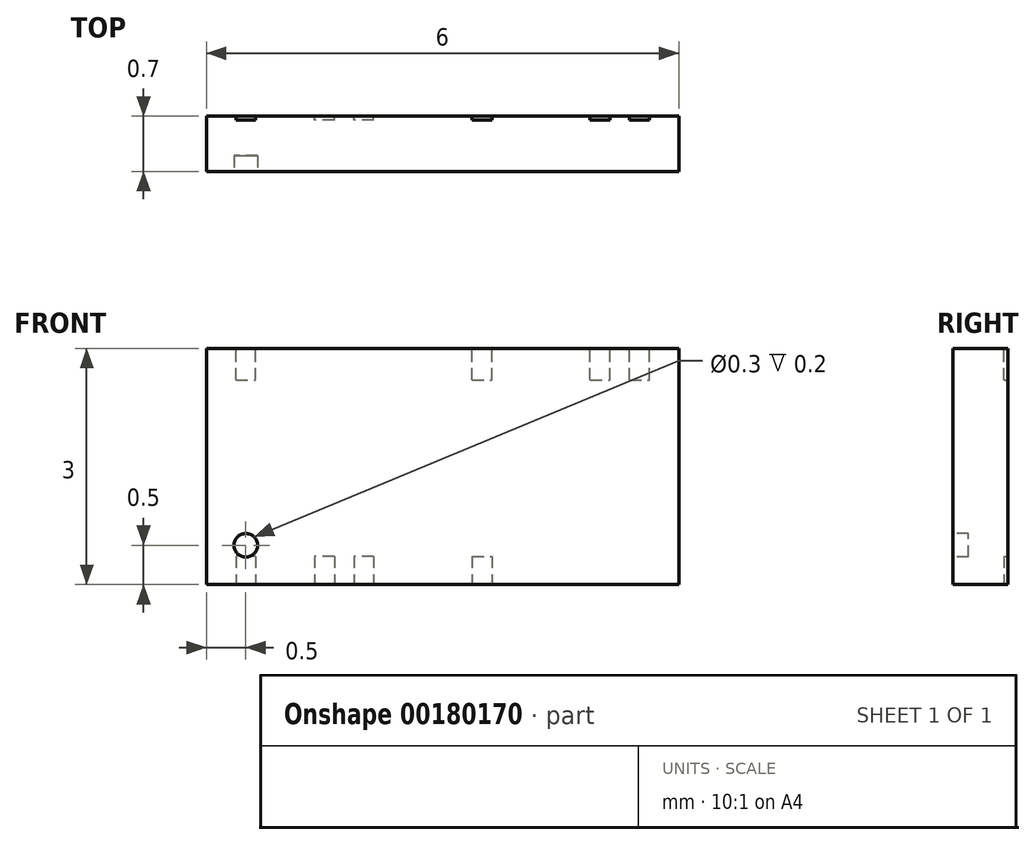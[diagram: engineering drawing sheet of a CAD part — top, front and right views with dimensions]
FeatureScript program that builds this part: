
annotation { "Feature Type Name" : "Feature", "Feature Type Description" : "" }
export const myFeature = defineFeature(function(context is Context, id is Id, definition is map)
    precondition{}
    {
        {
            var Q0;
            Q0=qCreatedBy(makeId("Front.planeOp"),FACE);
            var sketch = newSketch(context, id + "F0", { "sketchPlane" : qUnion([Q0])});
            skLineSegment(sketch, "E0.bottom", {"start": v(3, 1.5) * mm, "end": v(-3, 1.5) * mm});
            skLineSegment(sketch, "E0.top", {"start": v(3, -1.5) * mm, "end": v(-3, -1.5) * mm});
            skLineSegment(sketch, "E0.left", {"start": v(3, 1.5) * mm, "end": v(3, -1.5) * mm});
            skLineSegment(sketch, "E0.right", {"start": v(-3, 1.5) * mm, "end": v(-3, -1.5) * mm});
            skPoint(sketch, "E0.middle", {"position": v(0, 0) * mm});
            skSolve(sketch);
        }
        {
            var Q0;
            Q0 = qSketchRegion(id + "F0", true);
            extrude(context, id + "F1", {"entities" : qUnion([Q0]), "depth" : 0.7 * mm});
        }
        {
            var Q0;
            Q0=makeQuery(id+"F1.opExtrude","CAP_FACE",FACE,{"disambiguationData":[OSD([sQuery(id+"F0.wireOp",EDGE,"E0.bottom"),sQuery(id+"F0.wireOp",EDGE,"E0.top"),sQuery(id+"F0.wireOp",EDGE,"E0.left"),sQuery(id+"F0.wireOp",EDGE,"E0.right")])],"isStart":false});
            var sketch = newSketch(context, id + "F2", { "sketchPlane" : qUnion([Q0])});
            skCircle(sketch, "E1", {"center": v(-2.5, -1) * mm, "radius": 0.15 * mm});
            skSolve(sketch);
        }
        {
            var Q0;
            Q0 = qSketchRegion(id + "F2", true);
            extrude(context, id + "F3", {"entities" : qUnion([Q0]), "operationType" : NewBodyOperationType.REMOVE, "oppositeDirection" : true, "depth" : 0.2 * mm});
        }
        {
            var Q0;
            Q0=makeQuery(id+"F1.opExtrude","CAP_FACE",FACE,{"disambiguationData":[OSD([sQuery(id+"F0.wireOp",EDGE,"E0.bottom"),sQuery(id+"F0.wireOp",EDGE,"E0.top"),sQuery(id+"F0.wireOp",EDGE,"E0.left"),sQuery(id+"F0.wireOp",EDGE,"E0.right")])],"isStart":true});
            var sketch = newSketch(context, id + "F4", { "sketchPlane" : qUnion([Q0])});
            skLineSegment(sketch, "E2.bottom", {"start": v(2.62, 1.1) * mm, "end": v(2.38, 1.1) * mm});
            skLineSegment(sketch, "E2.right", {"start": v(2.38, 1.1) * mm, "end": v(2.38, 1.5) * mm});
            skPoint(sketch, "E2.middle", {"position": v(2.5, 1.5) * mm});
            skLineSegment(sketch, "E3.bottom", {"start": v(2.37, -1.14) * mm, "end": v(2.62, -1.14) * mm});
            skLineSegment(sketch, "E3.left", {"start": v(2.38, -1.14) * mm, "end": v(2.38, -1.5) * mm});
            skPoint(sketch, "E3.middle", {"position": v(2.5, -1.5) * mm});
            skPoint(sketch, "E3.cornerSnap0", {"position": v(2.38, 1.5) * mm});
            skLineSegment(sketch, "E4.bottom", {"start": v(2.12, 1.1) * mm, "end": v(1.88, 1.1) * mm});
            skLineSegment(sketch, "E4.left", {"start": v(2.12, 1.1) * mm, "end": v(2.12, 1.5) * mm});
            skPoint(sketch, "E4.middle", {"position": v(2, 1.5) * mm});
            skLineSegment(sketch, "E5.bottom", {"start": v(1.88, -1.14) * mm, "end": v(2.13, -1.14) * mm});
            skLineSegment(sketch, "E5.left", {"start": v(1.88, -1.14) * mm, "end": v(1.88, -1.5) * mm});
            skPoint(sketch, "E5.middle", {"position": v(2, -1.5) * mm});
            skLineSegment(sketch, "E6.bottom", {"start": v(1.63, 1.1) * mm, "end": v(1.38, 1.1) * mm});
            skLineSegment(sketch, "E6.left", {"start": v(1.63, 1.1) * mm, "end": v(1.63, 1.5) * mm});
            skPoint(sketch, "E6.middle", {"position": v(1.5, 1.5) * mm});
            skLineSegment(sketch, "E7.bottom", {"start": v(1.38, -1.14) * mm, "end": v(1.62, -1.14) * mm});
            skLineSegment(sketch, "E7.left", {"start": v(1.38, -1.14) * mm, "end": v(1.38, -1.5) * mm});
            skPoint(sketch, "E7.middle", {"position": v(1.5, -1.5) * mm});
            skLineSegment(sketch, "E8.bottom", {"start": v(1.13, 1.1) * mm, "end": v(0.88, 1.1) * mm});
            skLineSegment(sketch, "E8.left", {"start": v(1.13, 1.1) * mm, "end": v(1.13, 1.5) * mm});
            skPoint(sketch, "E8.middle", {"position": v(1, 1.5) * mm});
            skLineSegment(sketch, "E9.bottom", {"start": v(0.88, -1.14) * mm, "end": v(1.13, -1.14) * mm});
            skLineSegment(sketch, "E9.left", {"start": v(0.87, -1.14) * mm, "end": v(0.87, -1.5) * mm});
            skPoint(sketch, "E9.middle", {"position": v(1, -1.5) * mm});
            skLineSegment(sketch, "E10.bottom", {"start": v(0.37, 1.1) * mm, "end": v(0.62, 1.1) * mm});
            skLineSegment(sketch, "E10.right", {"start": v(0.62, 1.1) * mm, "end": v(0.62, 1.5) * mm});
            skPoint(sketch, "E10.middle", {"position": v(0.5, 1.5) * mm});
            skLineSegment(sketch, "E11.bottom", {"start": v(0.38, -1.14) * mm, "end": v(0.62, -1.14) * mm});
            skLineSegment(sketch, "E11.left", {"start": v(0.38, -1.14) * mm, "end": v(0.38, -1.5) * mm});
            skPoint(sketch, "E11.middle", {"position": v(0.5, -1.5) * mm});
            skLineSegment(sketch, "E12.bottom", {"start": v(0.12, 1.1) * mm, "end": v(-0.13, 1.1) * mm});
            skLineSegment(sketch, "E12.left", {"start": v(0.13, 1.1) * mm, "end": v(0.13, 1.5) * mm});
            skPoint(sketch, "E12.middle", {"position": v(0, 1.5) * mm});
            skPoint(sketch, "E12.cornerSnap0", {"position": v(0.5, 1.1) * mm});
            skLineSegment(sketch, "E13.bottom", {"start": v(-0.12, -1.14) * mm, "end": v(0.13, -1.14) * mm});
            skLineSegment(sketch, "E13.left", {"start": v(-0.13, -1.14) * mm, "end": v(-0.13, -1.5) * mm});
            skPoint(sketch, "E13.middle", {"position": v(0, -1.5) * mm});
            skLineSegment(sketch, "E14.bottom", {"start": v(-0.38, 1.1) * mm, "end": v(-0.63, 1.1) * mm});
            skLineSegment(sketch, "E14.left", {"start": v(-0.37, 1.1) * mm, "end": v(-0.37, 1.5) * mm});
            skPoint(sketch, "E14.middle", {"position": v(-0.5, 1.5) * mm});
            skLineSegment(sketch, "E15.bottom", {"start": v(-0.37, -1.14) * mm, "end": v(-0.62, -1.14) * mm});
            skLineSegment(sketch, "E15.right", {"start": v(-0.62, -1.14) * mm, "end": v(-0.62, -1.5) * mm});
            skPoint(sketch, "E15.middle", {"position": v(-0.5, -1.5) * mm});
            skLineSegment(sketch, "E16.bottom", {"start": v(-0.88, 1.1) * mm, "end": v(-1.13, 1.1) * mm});
            skLineSegment(sketch, "E16.left", {"start": v(-0.88, 1.1) * mm, "end": v(-0.88, 1.5) * mm});
            skPoint(sketch, "E16.middle", {"position": v(-1, 1.5) * mm});
            skLineSegment(sketch, "E17.bottom", {"start": v(-0.87, -1.14) * mm, "end": v(-1.12, -1.14) * mm});
            skLineSegment(sketch, "E17.right", {"start": v(-1.12, -1.14) * mm, "end": v(-1.12, -1.5) * mm});
            skPoint(sketch, "E17.middle", {"position": v(-1, -1.5) * mm});
            skLineSegment(sketch, "E18.bottom", {"start": v(-1.38, 1.1) * mm, "end": v(-1.63, 1.1) * mm});
            skLineSegment(sketch, "E18.left", {"start": v(-1.38, 1.1) * mm, "end": v(-1.38, 1.5) * mm});
            skPoint(sketch, "E18.middle", {"position": v(-1.5, 1.5) * mm});
            skLineSegment(sketch, "E19.bottom", {"start": v(-1.37, -1.14) * mm, "end": v(-1.62, -1.14) * mm});
            skLineSegment(sketch, "E19.right", {"start": v(-1.62, -1.14) * mm, "end": v(-1.62, -1.5) * mm});
            skPoint(sketch, "E19.middle", {"position": v(-1.5, -1.5) * mm});
            skLineSegment(sketch, "E20.bottom", {"start": v(-1.88, 1.1) * mm, "end": v(-2.12, 1.1) * mm});
            skLineSegment(sketch, "E20.left", {"start": v(-1.88, 1.1) * mm, "end": v(-1.88, 1.5) * mm});
            skPoint(sketch, "E20.middle", {"position": v(-2, 1.5) * mm});
            skLineSegment(sketch, "E21.bottom", {"start": v(-1.88, -1.14) * mm, "end": v(-2.12, -1.14) * mm});
            skLineSegment(sketch, "E21.right", {"start": v(-2.12, -1.14) * mm, "end": v(-2.12, -1.5) * mm});
            skPoint(sketch, "E21.middle", {"position": v(-2, -1.5) * mm});
            skLineSegment(sketch, "E22.bottom", {"start": v(-2.38, 1.1) * mm, "end": v(-2.63, 1.1) * mm});
            skLineSegment(sketch, "E22.left", {"start": v(-2.37, 1.1) * mm, "end": v(-2.37, 1.5) * mm});
            skPoint(sketch, "E22.middle", {"position": v(-2.5, 1.5) * mm});
            skLineSegment(sketch, "E23.bottom", {"start": v(-2.37, -1.14) * mm, "end": v(-2.62, -1.14) * mm});
            skLineSegment(sketch, "E23.right", {"start": v(-2.62, -1.14) * mm, "end": v(-2.62, -1.5) * mm});
            skPoint(sketch, "E23.middle", {"position": v(-2.5, -1.5) * mm});
            skPoint(sketch, "E24.orphan", {"position": v(2.38, 1.9) * mm});
            skPoint(sketch, "E2.left.end.orphan", {"position": v(2.62, 1.9) * mm});
            skLineSegment(sketch, "E25.top", {"start": v(2.62, 1.5) * mm, "end": v(2.38, 1.5) * mm});
            skLineSegment(sketch, "E25.left", {"start": v(2.62, 1.1) * mm, "end": v(2.62, 1.5) * mm});
            skLineSegment(sketch, "E26.bottom", {"start": v(1.88, 1.1) * mm, "end": v(2.12, 1.1) * mm});
            skLineSegment(sketch, "E26.top", {"start": v(1.88, 1.5) * mm, "end": v(2.12, 1.5) * mm});
            skLineSegment(sketch, "E26.left", {"start": v(1.88, 1.1) * mm, "end": v(1.88, 1.5) * mm});
            skLineSegment(sketch, "E27.bottom", {"start": v(1.38, 1.1) * mm, "end": v(1.63, 1.1) * mm});
            skLineSegment(sketch, "E27.top", {"start": v(1.38, 1.5) * mm, "end": v(1.63, 1.5) * mm});
            skLineSegment(sketch, "E27.left", {"start": v(1.38, 1.1) * mm, "end": v(1.38, 1.5) * mm});
            skLineSegment(sketch, "E28.bottom", {"start": v(0.88, 1.1) * mm, "end": v(1.13, 1.1) * mm});
            skLineSegment(sketch, "E28.top", {"start": v(0.88, 1.5) * mm, "end": v(1.12, 1.5) * mm});
            skLineSegment(sketch, "E28.left", {"start": v(0.88, 1.1) * mm, "end": v(0.88, 1.5) * mm});
            skLineSegment(sketch, "E28.right", {"start": v(1.12, 1.1) * mm, "end": v(1.12, 1.5) * mm});
            skPoint(sketch, "E29.orphan", {"position": v(1.87, 1.9) * mm});
            skPoint(sketch, "E30.orphan", {"position": v(2.12, 1.9) * mm});
            skPoint(sketch, "E31.orphan", {"position": v(1.38, 1.9) * mm});
            skPoint(sketch, "E32.orphan", {"position": v(1.63, 1.9) * mm});
            skPoint(sketch, "E33.orphan", {"position": v(0.87, 1.9) * mm});
            skPoint(sketch, "E34.orphan", {"position": v(1.13, 1.9) * mm});
            skLineSegment(sketch, "E35.bottom", {"start": v(0.62, 1.1) * mm, "end": v(0.38, 1.1) * mm});
            skLineSegment(sketch, "E35.top", {"start": v(0.62, 1.5) * mm, "end": v(0.38, 1.5) * mm});
            skLineSegment(sketch, "E35.right", {"start": v(0.38, 1.1) * mm, "end": v(0.38, 1.5) * mm});
            skLineSegment(sketch, "E36.bottom", {"start": v(0.12, 1.1) * mm, "end": v(-0.12, 1.1) * mm});
            skLineSegment(sketch, "E36.top", {"start": v(0.12, 1.5) * mm, "end": v(-0.12, 1.5) * mm});
            skLineSegment(sketch, "E36.left", {"start": v(0.12, 1.1) * mm, "end": v(0.12, 1.5) * mm});
            skLineSegment(sketch, "E36.right", {"start": v(-0.12, 1.1) * mm, "end": v(-0.12, 1.5) * mm});
            skLineSegment(sketch, "E37.top", {"start": v(-0.38, 1.5) * mm, "end": v(-0.63, 1.5) * mm});
            skLineSegment(sketch, "E37.left", {"start": v(-0.38, 1.1) * mm, "end": v(-0.38, 1.5) * mm});
            skLineSegment(sketch, "E37.right", {"start": v(-0.63, 1.1) * mm, "end": v(-0.63, 1.5) * mm});
            skLineSegment(sketch, "E38.bottom", {"start": v(-0.88, 1.1) * mm, "end": v(-1.12, 1.1) * mm});
            skLineSegment(sketch, "E38.top", {"start": v(-0.87, 1.5) * mm, "end": v(-1.12, 1.5) * mm});
            skLineSegment(sketch, "E38.left", {"start": v(-0.87, 1.1) * mm, "end": v(-0.87, 1.5) * mm});
            skLineSegment(sketch, "E38.right", {"start": v(-1.12, 1.1) * mm, "end": v(-1.12, 1.5) * mm});
            skLineSegment(sketch, "E39.bottom", {"start": v(-1.38, 1.1) * mm, "end": v(-1.62, 1.1) * mm});
            skLineSegment(sketch, "E39.top", {"start": v(-1.38, 1.5) * mm, "end": v(-1.62, 1.5) * mm});
            skLineSegment(sketch, "E39.right", {"start": v(-1.62, 1.1) * mm, "end": v(-1.62, 1.5) * mm});
            skLineSegment(sketch, "E40.bottom", {"start": v(-1.88, 1.1) * mm, "end": v(-2.13, 1.1) * mm});
            skLineSegment(sketch, "E40.top", {"start": v(-1.88, 1.5) * mm, "end": v(-2.13, 1.5) * mm});
            skLineSegment(sketch, "E40.right", {"start": v(-2.13, 1.1) * mm, "end": v(-2.13, 1.5) * mm});
            skLineSegment(sketch, "E41.top", {"start": v(-2.38, 1.5) * mm, "end": v(-2.63, 1.5) * mm});
            skLineSegment(sketch, "E41.left", {"start": v(-2.38, 1.1) * mm, "end": v(-2.38, 1.5) * mm});
            skLineSegment(sketch, "E41.right", {"start": v(-2.63, 1.1) * mm, "end": v(-2.63, 1.5) * mm});
            skPoint(sketch, "E42.orphan", {"position": v(0.38, 1.9) * mm});
            skPoint(sketch, "E43.orphan", {"position": v(0.62, 1.9) * mm});
            skPoint(sketch, "E12.top.end.orphan", {"position": v(-0.12, 1.9) * mm});
            skPoint(sketch, "E44.orphan", {"position": v(0.13, 1.9) * mm});
            skPoint(sketch, "E45.orphan", {"position": v(-0.62, 1.9) * mm});
            skPoint(sketch, "E46.orphan", {"position": v(-0.37, 1.9) * mm});
            skPoint(sketch, "E47.orphan", {"position": v(-1.12, 1.9) * mm});
            skPoint(sketch, "E48.orphan", {"position": v(-0.88, 1.9) * mm});
            skPoint(sketch, "E49.orphan", {"position": v(-1.62, 1.9) * mm});
            skPoint(sketch, "E50.orphan", {"position": v(-1.38, 1.9) * mm});
            skPoint(sketch, "E51.orphan", {"position": v(-2.13, 1.9) * mm});
            skPoint(sketch, "E52.orphan", {"position": v(-1.88, 1.9) * mm});
            skPoint(sketch, "E53.orphan", {"position": v(-2.62, 1.9) * mm});
            skPoint(sketch, "E54.orphan", {"position": v(-2.37, 1.9) * mm});
            skLineSegment(sketch, "E55.bottom", {"start": v(2.37, -1.14) * mm, "end": v(2.63, -1.14) * mm});
            skLineSegment(sketch, "E55.top", {"start": v(2.37, -1.5) * mm, "end": v(2.63, -1.5) * mm});
            skLineSegment(sketch, "E55.left", {"start": v(2.37, -1.14) * mm, "end": v(2.37, -1.5) * mm});
            skLineSegment(sketch, "E55.right", {"start": v(2.63, -1.14) * mm, "end": v(2.63, -1.5) * mm});
            skLineSegment(sketch, "E56.bottom", {"start": v(1.88, -1.14) * mm, "end": v(2.12, -1.14) * mm});
            skLineSegment(sketch, "E56.top", {"start": v(1.88, -1.5) * mm, "end": v(2.12, -1.5) * mm});
            skLineSegment(sketch, "E56.right", {"start": v(2.12, -1.14) * mm, "end": v(2.12, -1.5) * mm});
            skLineSegment(sketch, "E57.top", {"start": v(1.38, -1.5) * mm, "end": v(1.62, -1.5) * mm});
            skLineSegment(sketch, "E57.right", {"start": v(1.62, -1.14) * mm, "end": v(1.62, -1.5) * mm});
            skLineSegment(sketch, "E58.top", {"start": v(0.88, -1.5) * mm, "end": v(1.13, -1.5) * mm});
            skLineSegment(sketch, "E58.left", {"start": v(0.88, -1.14) * mm, "end": v(0.88, -1.5) * mm});
            skLineSegment(sketch, "E58.right", {"start": v(1.13, -1.14) * mm, "end": v(1.13, -1.5) * mm});
            skLineSegment(sketch, "E59.top", {"start": v(0.38, -1.5) * mm, "end": v(0.62, -1.5) * mm});
            skLineSegment(sketch, "E59.right", {"start": v(0.62, -1.14) * mm, "end": v(0.62, -1.5) * mm});
            skLineSegment(sketch, "E60.bottom", {"start": v(-0.12, -1.14) * mm, "end": v(0.12, -1.14) * mm});
            skLineSegment(sketch, "E60.top", {"start": v(-0.12, -1.5) * mm, "end": v(0.12, -1.5) * mm});
            skLineSegment(sketch, "E60.left", {"start": v(-0.12, -1.14) * mm, "end": v(-0.12, -1.5) * mm});
            skLineSegment(sketch, "E60.right", {"start": v(0.12, -1.14) * mm, "end": v(0.12, -1.5) * mm});
            skPoint(sketch, "E61.orphan", {"position": v(2.62, -1.86) * mm});
            skPoint(sketch, "E62.orphan", {"position": v(2.38, -1.86) * mm});
            skPoint(sketch, "E63.orphan", {"position": v(2.12, -1.86) * mm});
            skPoint(sketch, "E64.orphan", {"position": v(1.88, -1.86) * mm});
            skPoint(sketch, "E65.orphan", {"position": v(1.62, -1.86) * mm});
            skPoint(sketch, "E66.orphan", {"position": v(1.38, -1.86) * mm});
            skPoint(sketch, "E67.orphan", {"position": v(1.13, -1.86) * mm});
            skPoint(sketch, "E68.orphan", {"position": v(0.87, -1.86) * mm});
            skPoint(sketch, "E69.orphan", {"position": v(0.62, -1.86) * mm});
            skPoint(sketch, "E70.orphan", {"position": v(0.38, -1.86) * mm});
            skPoint(sketch, "E13.top.end.orphan", {"position": v(0.13, -1.86) * mm});
            skPoint(sketch, "E71.orphan", {"position": v(-0.13, -1.86) * mm});
            skLineSegment(sketch, "E72.bottom", {"start": v(-0.62, -1.14) * mm, "end": v(-0.37, -1.14) * mm});
            skLineSegment(sketch, "E72.top", {"start": v(-0.62, -1.5) * mm, "end": v(-0.37, -1.5) * mm});
            skLineSegment(sketch, "E72.right", {"start": v(-0.37, -1.14) * mm, "end": v(-0.37, -1.5) * mm});
            skLineSegment(sketch, "E73.bottom", {"start": v(-1.12, -1.14) * mm, "end": v(-0.88, -1.14) * mm});
            skLineSegment(sketch, "E73.top", {"start": v(-1.12, -1.5) * mm, "end": v(-0.88, -1.5) * mm});
            skLineSegment(sketch, "E73.right", {"start": v(-0.88, -1.14) * mm, "end": v(-0.88, -1.5) * mm});
            skLineSegment(sketch, "E74.bottom", {"start": v(-1.62, -1.14) * mm, "end": v(-1.38, -1.14) * mm});
            skLineSegment(sketch, "E74.top", {"start": v(-1.62, -1.5) * mm, "end": v(-1.38, -1.5) * mm});
            skLineSegment(sketch, "E74.right", {"start": v(-1.38, -1.14) * mm, "end": v(-1.38, -1.5) * mm});
            skLineSegment(sketch, "E75.bottom", {"start": v(-2.12, -1.14) * mm, "end": v(-1.88, -1.14) * mm});
            skLineSegment(sketch, "E75.top", {"start": v(-2.12, -1.5) * mm, "end": v(-1.88, -1.5) * mm});
            skLineSegment(sketch, "E75.right", {"start": v(-1.88, -1.14) * mm, "end": v(-1.88, -1.5) * mm});
            skLineSegment(sketch, "E76.bottom", {"start": v(-2.62, -1.14) * mm, "end": v(-2.38, -1.14) * mm});
            skLineSegment(sketch, "E76.top", {"start": v(-2.62, -1.5) * mm, "end": v(-2.38, -1.5) * mm});
            skLineSegment(sketch, "E76.right", {"start": v(-2.38, -1.14) * mm, "end": v(-2.38, -1.5) * mm});
            skPoint(sketch, "E77.orphan", {"position": v(-0.37, -1.86) * mm});
            skPoint(sketch, "E78.orphan", {"position": v(-0.62, -1.86) * mm});
            skPoint(sketch, "E79.orphan", {"position": v(-0.87, -1.86) * mm});
            skPoint(sketch, "E80.orphan", {"position": v(-1.12, -1.86) * mm});
            skPoint(sketch, "E81.orphan", {"position": v(-1.37, -1.86) * mm});
            skPoint(sketch, "E82.orphan", {"position": v(-1.62, -1.86) * mm});
            skPoint(sketch, "E83.orphan", {"position": v(-1.88, -1.86) * mm});
            skPoint(sketch, "E84.orphan", {"position": v(-2.12, -1.86) * mm});
            skPoint(sketch, "E85.orphan", {"position": v(-2.38, -1.86) * mm});
            skPoint(sketch, "E86.orphan", {"position": v(-2.62, -1.86) * mm});
            skSolve(sketch);
        }
        {
            var Q0;
            Q0=makeQuery(id+"F4.imprint","IMPRINT",FACE,{"disambiguationData":[TD([[makeQuery(id+"F4.imprint","IMPRINT",EDGE,{"derivedFrom":sQuery(id+"F4.wireOp",EDGE,"E55.top")}),1.0]])]});
            var Q1;
            Q1=makeQuery(id+"F4.imprint","IMPRINT",FACE,{"disambiguationData":[TD([[makeQuery(id+"F4.imprint","IMPRINT",EDGE,{"derivedFrom":sQuery(id+"F4.wireOp",EDGE,"E56.bottom")}),-1.0]])]});
            var Q2;
            Q2=makeQuery(id+"F4.imprint","IMPRINT",FACE,{"disambiguationData":[TD([[makeQuery(id+"F4.imprint","IMPRINT",EDGE,{"derivedFrom":sQuery(id+"F4.wireOp",EDGE,"E7.bottom")}),-1.0]])]});
            var Q3;
            Q3=makeQuery(id+"F4.imprint","IMPRINT",FACE,{"disambiguationData":[TD([[makeQuery(id+"F4.imprint","IMPRINT",EDGE,{"derivedFrom":sQuery(id+"F4.wireOp",EDGE,"E9.bottom")}),-1.0]])]});
            var Q4;
            Q4=makeQuery(id+"F4.imprint","IMPRINT",FACE,{"disambiguationData":[TD([[makeQuery(id+"F4.imprint","IMPRINT",EDGE,{"derivedFrom":sQuery(id+"F4.wireOp",EDGE,"E11.bottom")}),-1.0]])]});
            var Q5;
            Q5=makeQuery(id+"F4.imprint","IMPRINT",FACE,{"disambiguationData":[TD([[makeQuery(id+"F4.imprint","IMPRINT",EDGE,{"derivedFrom":sQuery(id+"F4.wireOp",EDGE,"E60.bottom")}),-1.0]])]});
            var Q6;
            Q6=makeQuery(id+"F4.imprint","IMPRINT",FACE,{"disambiguationData":[TD([[makeQuery(id+"F4.imprint","IMPRINT",EDGE,{"derivedFrom":sQuery(id+"F4.wireOp",EDGE,"E72.top")}),1.0]])]});
            var Q7;
            Q7=makeQuery(id+"F4.imprint","IMPRINT",FACE,{"disambiguationData":[TD([[makeQuery(id+"F4.imprint","IMPRINT",EDGE,{"derivedFrom":sQuery(id+"F4.wireOp",EDGE,"E73.bottom")}),-1.0]])]});
            var Q8;
            Q8=makeQuery(id+"F4.imprint","IMPRINT",FACE,{"disambiguationData":[TD([[makeQuery(id+"F4.imprint","IMPRINT",EDGE,{"derivedFrom":sQuery(id+"F4.wireOp",EDGE,"E74.bottom")}),-1.0]])]});
            var Q9;
            Q9=makeQuery(id+"F4.imprint","IMPRINT",FACE,{"disambiguationData":[TD([[makeQuery(id+"F4.imprint","IMPRINT",EDGE,{"derivedFrom":sQuery(id+"F4.wireOp",EDGE,"E75.bottom")}),-1.0]])]});
            var Q10;
            Q10=makeQuery(id+"F4.imprint","IMPRINT",FACE,{"disambiguationData":[TD([[makeQuery(id+"F4.imprint","IMPRINT",EDGE,{"derivedFrom":sQuery(id+"F4.wireOp",EDGE,"E76.bottom")}),-1.0]])]});
            var Q11;
            Q11=makeQuery(id+"F4.imprint","IMPRINT",FACE,{"disambiguationData":[TD([[makeQuery(id+"F4.imprint","IMPRINT",EDGE,{"derivedFrom":sQuery(id+"F4.wireOp",EDGE,"E41.top")}),-1.0]])]});
            var Q12;
            Q12=makeQuery(id+"F4.imprint","IMPRINT",FACE,{"disambiguationData":[TD([[makeQuery(id+"F4.imprint","IMPRINT",EDGE,{"derivedFrom":sQuery(id+"F4.wireOp",EDGE,"E40.top")}),-1.0]])]});
            var Q13;
            Q13=makeQuery(id+"F4.imprint","IMPRINT",FACE,{"disambiguationData":[TD([[makeQuery(id+"F4.imprint","IMPRINT",EDGE,{"derivedFrom":sQuery(id+"F4.wireOp",EDGE,"E39.bottom")}),-1.0]])]});
            var Q14;
            Q14=makeQuery(id+"F4.imprint","IMPRINT",FACE,{"disambiguationData":[TD([[makeQuery(id+"F4.imprint","IMPRINT",EDGE,{"derivedFrom":sQuery(id+"F4.wireOp",EDGE,"E38.bottom")}),-1.0]])]});
            var Q15;
            Q15=makeQuery(id+"F4.imprint","IMPRINT",FACE,{"disambiguationData":[TD([[makeQuery(id+"F4.imprint","IMPRINT",EDGE,{"derivedFrom":sQuery(id+"F4.wireOp",EDGE,"E37.top")}),-1.0]])]});
            var Q16;
            Q16=makeQuery(id+"F4.imprint","IMPRINT",FACE,{"disambiguationData":[TD([[makeQuery(id+"F4.imprint","IMPRINT",EDGE,{"derivedFrom":sQuery(id+"F4.wireOp",EDGE,"E36.bottom")}),-1.0]])]});
            var Q17;
            Q17=makeQuery(id+"F4.imprint","IMPRINT",FACE,{"disambiguationData":[TD([[makeQuery(id+"F4.imprint","IMPRINT",EDGE,{"derivedFrom":sQuery(id+"F4.wireOp",EDGE,"E35.bottom")}),-1.0]])]});
            var Q18;
            Q18=makeQuery(id+"F4.imprint","IMPRINT",FACE,{"disambiguationData":[TD([[makeQuery(id+"F4.imprint","IMPRINT",EDGE,{"derivedFrom":sQuery(id+"F4.wireOp",EDGE,"E28.bottom")}),1.0]])]});
            var Q19;
            Q19=makeQuery(id+"F4.imprint","IMPRINT",FACE,{"disambiguationData":[TD([[makeQuery(id+"F4.imprint","IMPRINT",EDGE,{"derivedFrom":sQuery(id+"F4.wireOp",EDGE,"E27.bottom")}),1.0]])]});
            var Q20;
            Q20=makeQuery(id+"F4.imprint","IMPRINT",FACE,{"disambiguationData":[TD([[makeQuery(id+"F4.imprint","IMPRINT",EDGE,{"derivedFrom":sQuery(id+"F4.wireOp",EDGE,"E26.bottom")}),1.0]])]});
            var Q21;
            Q21=makeQuery(id+"F4.imprint","IMPRINT",FACE,{"disambiguationData":[TD([[makeQuery(id+"F4.imprint","IMPRINT",EDGE,{"derivedFrom":sQuery(id+"F4.wireOp",EDGE,"E2.bottom")}),-1.0]])]});
            extrude(context, id + "F5", {"entities" : qUnion([Q0, Q1, Q2, Q3, Q4, Q5, Q6, Q7, Q8, Q9, Q10, Q11, Q12, Q13, Q14, Q15, Q16, Q17, Q18, Q19, Q20, Q21]), "operationType" : NewBodyOperationType.REMOVE, "oppositeDirection" : true, "depth" : 0.05 * mm});
        }
    });
